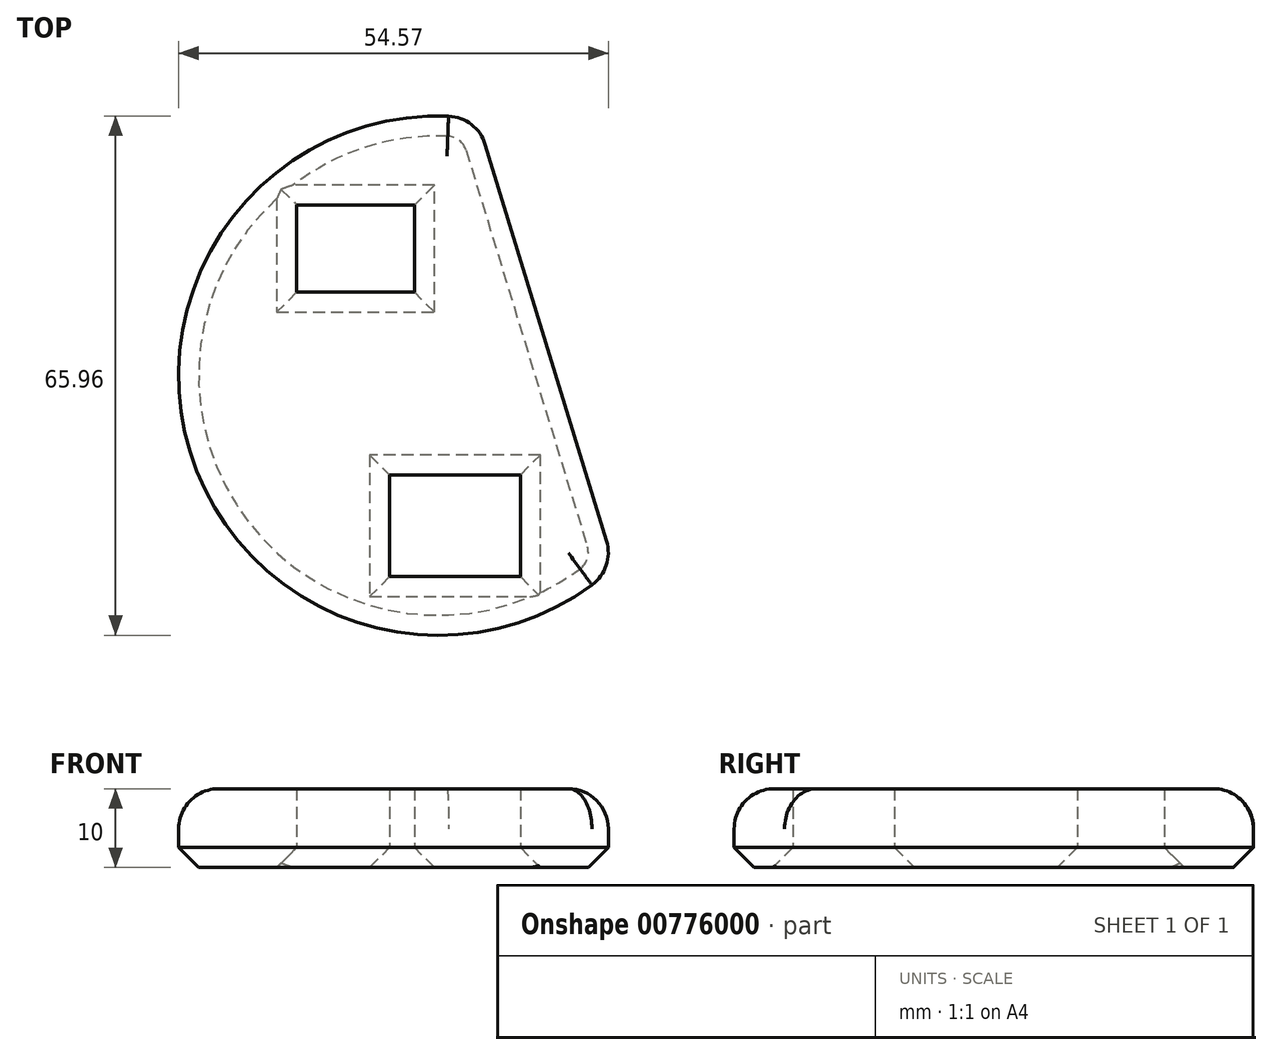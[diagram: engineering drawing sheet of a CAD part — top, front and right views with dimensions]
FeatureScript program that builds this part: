
annotation { "Feature Type Name" : "Feature", "Feature Type Description" : "" }
export const myFeature = defineFeature(function(context is Context, id is Id, definition is map)
    precondition{}
    {
        {
            var Q0;
            Q0=qCreatedBy(makeId("Top.planeOp"),FACE);
            var sketch = newSketch(context, id + "F0", { "sketchPlane" : qUnion([Q0])});
            skArc(sketch, "E0", {"start": v(4.97, 32.6) * mm, "mid": v(-31.54, -9.65) * mm, "end": v(22.36, -24.25) * mm});
            skLineSegment(sketch, "E1.bottom", {"start": v(-17.97, 10.6) * mm, "end": v(-3.04, 10.6) * mm});
            skLineSegment(sketch, "E1.top", {"start": v(-17.97, 21.66) * mm, "end": v(-3.04, 21.66) * mm});
            skLineSegment(sketch, "E1.left", {"start": v(-17.97, 10.6) * mm, "end": v(-17.97, 21.66) * mm});
            skLineSegment(sketch, "E1.right", {"start": v(-3.04, 10.6) * mm, "end": v(-3.04, 21.66) * mm});
            skLineSegment(sketch, "E2.bottom", {"start": v(-6.18, -25.53) * mm, "end": v(10.42, -25.53) * mm});
            skLineSegment(sketch, "E2.top", {"start": v(-6.18, -12.63) * mm, "end": v(10.42, -12.63) * mm});
            skLineSegment(sketch, "E2.left", {"start": v(-6.18, -25.53) * mm, "end": v(-6.18, -12.63) * mm});
            skLineSegment(sketch, "E2.right", {"start": v(10.42, -25.53) * mm, "end": v(10.42, -12.63) * mm});
            skLineSegment(sketch, "E3", {"start": v(4.97, 32.6) * mm, "end": v(22.36, -24.25) * mm});
            skSolve(sketch);
        }
        {
            var Q0;
            Q0 = qSketchRegion(id + "F0", true);
            extrude(context, id + "F1", {"entities" : qUnion([Q0]), "depth" : 10 * mm, "offsetDistance" : 25.4 * mm});
        }
        {
            var Q0;
            Q0=makeQuery(id+"F1.opExtrude","CAP_EDGE",EDGE,{"disambiguationData":[OSD([sQuery(id+"F0.wireOp",EDGE,"E0")])],"isStart":false});
            fillet(context, id + "F2", {"entities" : qUnion([Q0]), "radius" : 5.08 * mm, "tangentPropagation" : true, "allowEdgeOverflow" : false});
        }
        {
            var Q0;
            Q0=makeQuery(id+"F1.opExtrude","CAP_EDGE",EDGE,{"disambiguationData":[OSD([sQuery(id+"F0.wireOp",EDGE,"E3")])],"isStart":false});
            fillet(context, id + "F3", {"entities" : qUnion([Q0]), "radius" : 5.08 * mm, "tangentPropagation" : true, "allowEdgeOverflow" : false});
        }
        {
            var Q0;
            Q0=makeQuery(id+"F1.opExtrude","CAP_FACE",FACE,{"disambiguationData":[OSD([sQuery(id+"F0.wireOp",EDGE,"E0"),sQuery(id+"F0.wireOp",EDGE,"E1.bottom"),sQuery(id+"F0.wireOp",EDGE,"E1.top"),sQuery(id+"F0.wireOp",EDGE,"E1.left"),sQuery(id+"F0.wireOp",EDGE,"E1.right"),sQuery(id+"F0.wireOp",EDGE,"E2.bottom"),sQuery(id+"F0.wireOp",EDGE,"E2.top"),sQuery(id+"F0.wireOp",EDGE,"E2.left"),sQuery(id+"F0.wireOp",EDGE,"E2.right"),sQuery(id+"F0.wireOp",EDGE,"E3")])],"isStart":true});
            chamfer(context, id + "F4", {"entities" : qUnion([Q0]), "width" : 2.54 * mm, "tangentPropagation" : true});
        }
    });
